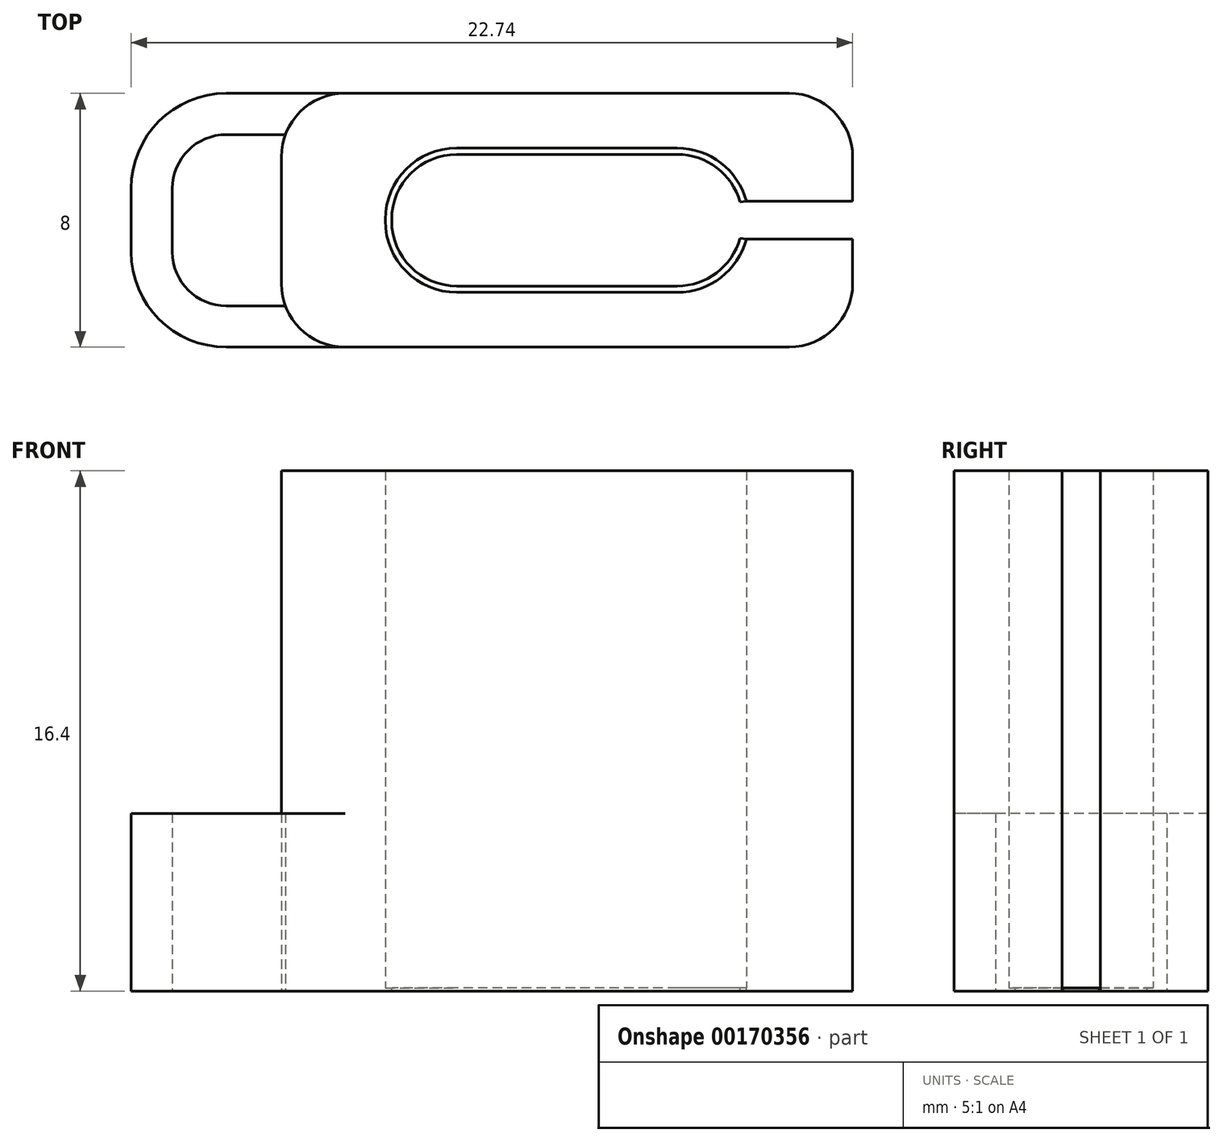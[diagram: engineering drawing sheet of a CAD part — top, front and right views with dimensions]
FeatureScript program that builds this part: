
annotation { "Feature Type Name" : "Feature", "Feature Type Description" : "" }
export const myFeature = defineFeature(function(context is Context, id is Id, definition is map)
    precondition{}
    {
        {
            var Q0;
            Q0=qCreatedBy(makeId("Top.planeOp"),FACE);
            var sketch = newSketch(context, id + "F0", { "sketchPlane" : qUnion([Q0])});
            skLineSegment(sketch, "E0.bottom", {"start": v(3.47, -2.27) * mm, "end": v(-3.47, -2.28) * mm});
            skLineSegment(sketch, "E0.top", {"start": v(3.47, 2.28) * mm, "end": v(-3.48, 2.27) * mm});
            skLineSegment(sketch, "E0.left", {"start": v(5.72, -0.02) * mm, "end": v(5.72, 0.03) * mm});
            skLineSegment(sketch, "E0.right", {"start": v(-5.72, -0.02) * mm, "end": v(-5.72, 0.02) * mm});
            skPoint(sketch, "E0.middle", {"position": v(0, 0) * mm});
            skPoint(sketch, "E1.visualSharp", {"position": v(-5.72, 2.27) * mm});
            skArc(sketch, "E1.filletArc", {"start": v(-3.48, 2.27) * mm, "mid": v(-5.07, 1.62) * mm, "end": v(-5.72, 0.02) * mm});
            skPoint(sketch, "E2.visualSharp", {"position": v(-5.72, -2.28) * mm});
            skArc(sketch, "E2.filletArc", {"start": v(-5.72, -0.03) * mm, "mid": v(-5.07, -1.62) * mm, "end": v(-3.47, -2.27) * mm});
            skPoint(sketch, "E3.visualSharp", {"position": v(5.72, -2.27) * mm});
            skArc(sketch, "E3.filletArc", {"start": v(3.47, -2.28) * mm, "mid": v(5.07, -1.62) * mm, "end": v(5.72, -0.02) * mm});
            skPoint(sketch, "E4.visualSharp", {"position": v(5.72, 2.28) * mm});
            skArc(sketch, "E4.filletArc", {"start": v(5.72, 0.03) * mm, "mid": v(5.07, 1.62) * mm, "end": v(3.47, 2.28) * mm});
            skLineSegment(sketch, "E5.bottom", {"start": v(4, -1.25) * mm, "end": v(-4, -1.25) * mm});
            skLineSegment(sketch, "E5.top", {"start": v(4, 1.25) * mm, "end": v(-4, 1.25) * mm});
            skLineSegment(sketch, "E5.left", {"start": v(4, -1.25) * mm, "end": v(4, 1.25) * mm});
            skLineSegment(sketch, "E5.right", {"start": v(-4, -1.25) * mm, "end": v(-4, 1.25) * mm});
            skSolve(sketch);
        }
        {
            var Q0;
            Q0=makeQuery(id+"F0.imprint","IMPRINT",FACE,{"disambiguationData":[TD([[makeQuery(id+"F0.imprint","IMPRINT",EDGE,{"derivedFrom":sQuery(id+"F0.wireOp",EDGE,"E0.bottom")}),-1.0]])]});
            var Q1;
            Q1=makeQuery(id+"F0.imprint","IMPRINT",FACE,{"disambiguationData":[TD([[makeQuery(id+"F0.imprint","IMPRINT",EDGE,{"derivedFrom":sQuery(id+"F0.wireOp",EDGE,"E5.bottom")}),-1.0]])]});
            extrude(context, id + "F1", {"entities" : qUnion([Q0, Q1]), "depth" : 16.25 * mm});
        }
        {
            var Q0;
            Q0=qCreatedBy(makeId("Top.planeOp"),FACE);
            var sketch = newSketch(context, id + "F2", { "sketchPlane" : qUnion([Q0])});
            skLineSegment(sketch, "E6.bottom", {"start": v(7, -4) * mm, "end": v(-7, -4) * mm});
            skLineSegment(sketch, "E6.top", {"start": v(7, 4) * mm, "end": v(-7, 4) * mm});
            skLineSegment(sketch, "E6.left", {"start": v(9, -2) * mm, "end": v(9, 2) * mm});
            skLineSegment(sketch, "E6.right", {"start": v(-9, -2) * mm, "end": v(-9, 2) * mm});
            skPoint(sketch, "E6.middle", {"position": v(0, 0) * mm});
            skPoint(sketch, "E7.visualSharp", {"position": v(-9, -4) * mm});
            skArc(sketch, "E7.filletArc", {"start": v(-9, -2) * mm, "mid": v(-8.41, -3.41) * mm, "end": v(-7, -4) * mm});
            skPoint(sketch, "E8.visualSharp", {"position": v(-9, 4) * mm});
            skArc(sketch, "E8.filletArc", {"start": v(-7, 4) * mm, "mid": v(-8.41, 3.41) * mm, "end": v(-9, 2) * mm});
            skPoint(sketch, "E9.visualSharp", {"position": v(9, -4) * mm});
            skArc(sketch, "E9.filletArc", {"start": v(7, -4) * mm, "mid": v(8.41, -3.41) * mm, "end": v(9, -2) * mm});
            skPoint(sketch, "E10.visualSharp", {"position": v(9, 4) * mm});
            skArc(sketch, "E10.filletArc", {"start": v(9, 2) * mm, "mid": v(8.41, 3.41) * mm, "end": v(7, 4) * mm});
            skLineSegment(sketch, "E11.bottom", {"start": v(-7, 4) * mm, "end": v(-10.74, 4) * mm});
            skLineSegment(sketch, "E11.top", {"start": v(-7, -4) * mm, "end": v(-10.74, -4) * mm});
            skLineSegment(sketch, "E11.left", {"start": v(-7, 4) * mm, "end": v(-7, -4) * mm});
            skLineSegment(sketch, "E11.right", {"start": v(-13.74, 1) * mm, "end": v(-13.74, -1) * mm});
            skPoint(sketch, "E12.visualSharp", {"position": v(-13.74, 4) * mm});
            skArc(sketch, "E12.filletArc", {"start": v(-10.74, 4) * mm, "mid": v(-12.86, 3.12) * mm, "end": v(-13.74, 1) * mm});
            skPoint(sketch, "E13.visualSharp", {"position": v(-13.74, -4) * mm});
            skArc(sketch, "E13.filletArc", {"start": v(-13.74, -1) * mm, "mid": v(-12.86, -3.12) * mm, "end": v(-10.74, -4) * mm});
            skArc(sketch, "E14.0", {"start": v(-12.44, -1) * mm, "mid": v(-11.94, -2.2) * mm, "end": v(-10.74, -2.7) * mm});
            skLineSegment(sketch, "E14.1", {"start": v(-12.44, 1) * mm, "end": v(-12.44, -1) * mm});
            skArc(sketch, "E14.2", {"start": v(-10.74, 2.7) * mm, "mid": v(-11.94, 2.2) * mm, "end": v(-12.44, 1) * mm});
            skLineSegment(sketch, "E15", {"start": v(-10.74, 2.7) * mm, "end": v(-7.92, 2.7) * mm});
            skLineSegment(sketch, "E16", {"start": v(-7.92, 2.7) * mm, "end": v(-7.92, -2.7) * mm});
            skLineSegment(sketch, "E17", {"start": v(-7.92, -2.7) * mm, "end": v(-10.74, -2.7) * mm});
            skSolve(sketch);
        }
        {
            var Q0;
            Q0=makeQuery(id+"F2.imprint","IMPRINT",FACE,{"disambiguationData":[TD([[makeQuery(id+"F2.imprint","IMPRINT",EDGE,{"derivedFrom":sQuery(id+"F2.wireOp",EDGE,"E6.bottom")}),-1.0]])]});
            var Q1;
            Q1=makeQuery(id+"F2.imprint","IMPRINT",FACE,{"disambiguationData":[TD([[makeQuery(id+"F2.imprint","IMPRINT",EDGE,{"derivedFrom":sQuery(id+"F2.wireOp",EDGE,"E6.right")}),-1.0]])]});
            var Q2;
            {var subQ0=sQuery(id+"F2.wireOp",EDGE,"E11.left");Q2=makeQuery(id+"F2.imprint","IMPRINT",FACE,{"disambiguationData":[TD([[makeQuery(id+"F2.imprint","IMPRINT",EDGE,{"derivedFrom":subQ0}),-1.0]])]});}
            extrude(context, id + "F3", {"entities" : qUnion([Q0, Q1, Q2]), "depth" : 16.2 * mm});
        }
        {
            var Q0;
            {var subQ0=sQuery(id+"F2.wireOp",EDGE,"E6.left");Q0=makeQuery(id+"FNUhWBLdZuZYwrX_2.boolean.opBoolean","MERGE",FACE,{"derivedFrom":[makeQuery(id+"F3.opExtrude","SWEPT_FACE",FACE,{"disambiguationData":[OSD([subQ0])]}),makeQuery(id+"FNUhWBLdZuZYwrX_2.opExtrude","SWEPT_FACE",FACE,{"disambiguationData":[OSD([subQ0])]})]});}
            var sketch = newSketch(context, id + "F4", { "sketchPlane" : qUnion([Q0])});
            skSolve(sketch);
        }
        {
            var Q0;
            {var subQ0=sQuery(id+"F2.wireOp",EDGE,"E6.left");Q0=makeQuery(id+"F4.imprint","IMPRINT",FACE,{"disambiguationData":[TD([[makeQuery(id+"F4.imprint","IMPRINT",EDGE,{"derivedFrom":makeQuery(id+"F3.opExtrude","CAP_EDGE",EDGE,{"disambiguationData":[OSD([subQ0])],"isStart":false})}),-1.0]])]});}
            var sketch = newSketch(context, id + "F5", { "sketchPlane" : qUnion([Q0])});
            skLineSegment(sketch, "E18.bottom", {"start": v(0.6, -1) * mm, "end": v(-0.6, -1) * mm});
            skLineSegment(sketch, "E18.top", {"start": v(0.6, 17) * mm, "end": v(-0.6, 17) * mm});
            skLineSegment(sketch, "E18.left", {"start": v(0.6, -1) * mm, "end": v(0.6, 17) * mm});
            skLineSegment(sketch, "E18.right", {"start": v(-0.6, -1) * mm, "end": v(-0.6, 17) * mm});
            skPoint(sketch, "E18.middle", {"position": v(0, 8) * mm});
            skLineSegment(sketch, "E19", {"start": v(-0.6, -1) * mm, "end": v(0.6, -1) * mm});
            skLineSegment(sketch, "E20", {"start": v(-0.6, 17) * mm, "end": v(0.6, 17) * mm});
            skSolve(sketch);
        }
        {
            var Q0;
            Q0=makeQuery(id+"F1.opExtrude","SWEPT_BODY",BODY,{"disambiguationData":[OSD([sQuery(id+"F0.wireOp",EDGE,"E0.bottom"),sQuery(id+"F0.wireOp",EDGE,"E0.top"),sQuery(id+"F0.wireOp",EDGE,"E0.left"),sQuery(id+"F0.wireOp",EDGE,"E0.right"),sQuery(id+"F0.wireOp",EDGE,"E1.filletArc"),sQuery(id+"F0.wireOp",EDGE,"E2.filletArc"),sQuery(id+"F0.wireOp",EDGE,"E3.filletArc"),sQuery(id+"F0.wireOp",EDGE,"E4.filletArc"),sQuery(id+"F0.wireOp",EDGE,"E5.bottom"),sQuery(id+"F0.wireOp",EDGE,"E5.top"),sQuery(id+"F0.wireOp",EDGE,"E5.left"),sQuery(id+"F0.wireOp",EDGE,"E5.right")])]});
            var Q1;
            Q1=makeQuery(id+"F3.opExtrude","SWEPT_BODY",BODY,{"disambiguationData":[OSD([sQuery(id+"F2.wireOp",EDGE,"E6.bottom"),sQuery(id+"F2.wireOp",EDGE,"E6.top"),sQuery(id+"F2.wireOp",EDGE,"E6.left"),sQuery(id+"F2.wireOp",EDGE,"E6.right"),sQuery(id+"F2.wireOp",EDGE,"E7.filletArc"),sQuery(id+"F2.wireOp",EDGE,"E8.filletArc"),sQuery(id+"F2.wireOp",EDGE,"E9.filletArc"),sQuery(id+"F2.wireOp",EDGE,"E10.filletArc")])]});
            booleanBodies(context, id + "F6", {"operationType" : BooleanOperationType.SUBTRACTION, "tools" : qUnion([Q0]), "targets" : qUnion([Q1])});
        }
        {
            var Q0;
            Q0 = qSketchRegion(id + "F5", true);
            extrude(context, id + "F7", {"entities" : qUnion([Q0]), "operationType" : NewBodyOperationType.REMOVE, "endBound" : BoundingType.UP_TO_NEXT, "oppositeDirection" : true, "depth" : 25 * mm});
        }
        {
            var Q0;
            {var subQ6=sQuery(id+"F2.wireOp",EDGE,"E11.bottom");Q0=makeQuery(id+"F2.imprint","IMPRINT",FACE,{"disambiguationData":[TD([[makeQuery(id+"F2.imprint","IMPRINT",EDGE,{"derivedFrom":subQ6}),1.0]])]});}
            extrude(context, id + "F8", {"entities" : qUnion([Q0]), "operationType" : NewBodyOperationType.ADD, "depth" : 5.5 * mm});
        }
        {
            var Q0;
            Q0=makeQuery(id+"F3.opExtrude","CAP_FACE",FACE,{"disambiguationData":[OSD([sQuery(id+"F2.wireOp",EDGE,"E6.bottom"),sQuery(id+"F2.wireOp",EDGE,"E6.top"),sQuery(id+"F2.wireOp",EDGE,"E6.left"),sQuery(id+"F2.wireOp",EDGE,"E6.right"),sQuery(id+"F2.wireOp",EDGE,"E7.filletArc"),sQuery(id+"F2.wireOp",EDGE,"E8.filletArc"),sQuery(id+"F2.wireOp",EDGE,"E9.filletArc"),sQuery(id+"F2.wireOp",EDGE,"E10.filletArc")])],"isStart":false});
            var sketch = newSketch(context, id + "F9", { "sketchPlane" : qUnion([Q0])});
            skArc(sketch, "E21.0", {"start": v(-3.47, -2.08) * mm, "mid": v(-4.92, -1.47) * mm, "end": v(-5.53, -0.03) * mm});
            skLineSegment(sketch, "E21.1", {"start": v(-3.47, -2.08) * mm, "end": v(3.47, -2.08) * mm});
            skArc(sketch, "E21.2", {"start": v(5.45, -0.57) * mm, "mid": v(4.72, -1.66) * mm, "end": v(3.47, -2.08) * mm});
            skArc(sketch, "E21.3", {"start": v(-5.53, 0.02) * mm, "mid": v(-4.92, 1.47) * mm, "end": v(-3.48, 2.08) * mm});
            skLineSegment(sketch, "E21.4", {"start": v(-3.48, 2.08) * mm, "end": v(3.47, 2.08) * mm});
            skArc(sketch, "E21.5", {"start": v(3.47, 2.08) * mm, "mid": v(4.72, 1.66) * mm, "end": v(5.45, 0.57) * mm});
            skArc(sketch, "E22.0", {"start": v(-7, 4) * mm, "mid": v(-8.41, 3.41) * mm, "end": v(-9, 2) * mm});
            skLineSegment(sketch, "E22.1", {"start": v(7, 4) * mm, "end": v(-7, 4) * mm});
            skLineSegment(sketch, "E22.2", {"start": v(-9, -2) * mm, "end": v(-9, 2) * mm});
            skArc(sketch, "E22.3", {"start": v(-9, -2) * mm, "mid": v(-8.41, -3.41) * mm, "end": v(-7, -4) * mm});
            skLineSegment(sketch, "E22.4", {"start": v(7, -4) * mm, "end": v(-7, -4) * mm});
            skArc(sketch, "E22.5", {"start": v(7, -4) * mm, "mid": v(8.41, -3.41) * mm, "end": v(9, -2) * mm});
            skLineSegment(sketch, "E22.6", {"start": v(9, -2) * mm, "end": v(9, -0.6) * mm});
            skArc(sketch, "E22.7", {"start": v(9, 2) * mm, "mid": v(8.41, 3.41) * mm, "end": v(7, 4) * mm});
            skLineSegment(sketch, "E22.8", {"start": v(9, 0.6) * mm, "end": v(9, 2) * mm});
            skLineSegment(sketch, "E23.0", {"start": v(5.65, 0.6) * mm, "end": v(9, 0.6) * mm});
            skLineSegment(sketch, "E24.0", {"start": v(5.65, -0.6) * mm, "end": v(9, -0.6) * mm});
            skLineSegment(sketch, "E25", {"start": v(5.65, 0.6) * mm, "end": v(5.45, 0.57) * mm});
            skLineSegment(sketch, "E26", {"start": v(5.65, -0.6) * mm, "end": v(5.45, -0.57) * mm});
            skLineSegment(sketch, "E27", {"start": v(-5.53, -0.03) * mm, "end": v(-5.53, 0.02) * mm});
            skSolve(sketch);
        }
        {
            var Q0;
            Q0=makeQuery(id+"F9.imprint","IMPRINT",FACE,{"disambiguationData":[TD([[makeQuery(id+"F9.imprint","IMPRINT",EDGE,{"derivedFrom":sQuery(id+"F9.wireOp",EDGE,"E21.0")}),1.0]])]});
            var Q1;
            Q1=makeQuery(id+"F9.imprint","IMPRINT",FACE,{"disambiguationData":[TD([[makeQuery(id+"F9.imprint","IMPRINT",EDGE,{"derivedFrom":sQuery(id+"F9.wireOp",EDGE,"E22.0")}),1.0]])]});
            extrude(context, id + "F10", {"entities" : qUnion([Q0, Q1]), "operationType" : NewBodyOperationType.ADD, "depth" : 0.1 * mm});
        }
        {
            var Q0;
            {var subQ0=sQuery(id+"F2.wireOp",EDGE,"E8.filletArc");var subQ1=sQuery(id+"F2.wireOp",EDGE,"E7.filletArc");Q0=makeQuery(id+"F8.boolean.opBoolean","MERGE",FACE,{"derivedFrom":[makeQuery(id+"F3.opExtrude","CAP_FACE",FACE,{"disambiguationData":[OSD([sQuery(id+"F2.wireOp",EDGE,"E6.bottom"),sQuery(id+"F2.wireOp",EDGE,"E6.top"),sQuery(id+"F2.wireOp",EDGE,"E6.left"),sQuery(id+"F2.wireOp",EDGE,"E6.right"),subQ1,subQ0,sQuery(id+"F2.wireOp",EDGE,"E9.filletArc"),sQuery(id+"F2.wireOp",EDGE,"E10.filletArc")])],"isStart":true}),makeQuery(id+"F8.opExtrude","CAP_FACE",FACE,{"disambiguationData":[OSD([subQ1,subQ0,sQuery(id+"F2.wireOp",EDGE,"E11.bottom"),sQuery(id+"F2.wireOp",EDGE,"E11.top"),sQuery(id+"F2.wireOp",EDGE,"E11.right"),sQuery(id+"F2.wireOp",EDGE,"E12.filletArc"),sQuery(id+"F2.wireOp",EDGE,"E13.filletArc"),sQuery(id+"F2.wireOp",EDGE,"E14.0"),sQuery(id+"F2.wireOp",EDGE,"E14.1"),sQuery(id+"F2.wireOp",EDGE,"E14.2"),sQuery(id+"F2.wireOp",EDGE,"E15"),sQuery(id+"F2.wireOp",EDGE,"E17")])],"isStart":true})]});}
            var sketch = newSketch(context, id + "F11", { "sketchPlane" : qUnion([Q0])});
            skArc(sketch, "E28.0", {"start": v(3.47, -2.08) * mm, "mid": v(4.72, -1.66) * mm, "end": v(5.45, -0.57) * mm});
            skLineSegment(sketch, "E28.1", {"start": v(-3.48, -2.08) * mm, "end": v(3.47, -2.08) * mm});
            skArc(sketch, "E28.2", {"start": v(-5.53, -0.02) * mm, "mid": v(-4.92, -1.47) * mm, "end": v(-3.48, -2.08) * mm});
            skArc(sketch, "E28.3", {"start": v(-3.47, 2.08) * mm, "mid": v(-4.92, 1.47) * mm, "end": v(-5.53, 0.03) * mm});
            skLineSegment(sketch, "E28.4", {"start": v(-3.47, 2.08) * mm, "end": v(3.47, 2.08) * mm});
            skArc(sketch, "E28.5", {"start": v(5.45, 0.57) * mm, "mid": v(4.72, 1.66) * mm, "end": v(3.47, 2.08) * mm});
            skLineSegment(sketch, "E29.2", {"start": v(-5.53, 0.03) * mm, "end": v(-5.53, -0.02) * mm});
            skLineSegment(sketch, "E30.0", {"start": v(5.65, -0.6) * mm, "end": v(9, -0.6) * mm});
            skLineSegment(sketch, "E31.0", {"start": v(5.65, 0.6) * mm, "end": v(9, 0.6) * mm});
            skLineSegment(sketch, "E32.0", {"start": v(5.65, 0.6) * mm, "end": v(5.45, 0.57) * mm});
            skLineSegment(sketch, "E33.0", {"start": v(5.65, -0.6) * mm, "end": v(5.45, -0.57) * mm});
            skLineSegment(sketch, "E34.0", {"start": v(9, 2) * mm, "end": v(9, 0.6) * mm});
            skArc(sketch, "E35.0", {"start": v(7, 4) * mm, "mid": v(8.41, 3.41) * mm, "end": v(9, 2) * mm});
            skLineSegment(sketch, "E36.0", {"start": v(9, -0.6) * mm, "end": v(9, -2) * mm});
            skArc(sketch, "E37.0", {"start": v(9, -2) * mm, "mid": v(8.41, -3.41) * mm, "end": v(7, -4) * mm});
            skLineSegment(sketch, "E38.0", {"start": v(7, -4) * mm, "end": v(-7, -4) * mm});
            skArc(sketch, "E39.0", {"start": v(-10.74, -4) * mm, "mid": v(-12.86, -3.12) * mm, "end": v(-13.74, -1) * mm});
            skLineSegment(sketch, "E40.0", {"start": v(-7, -4) * mm, "end": v(-10.74, -4) * mm});
            skLineSegment(sketch, "E41.0", {"start": v(-13.74, -1) * mm, "end": v(-13.74, 1) * mm});
            skArc(sketch, "E42.0", {"start": v(-13.74, 1) * mm, "mid": v(-12.86, 3.12) * mm, "end": v(-10.74, 4) * mm});
            skLineSegment(sketch, "E43.0", {"start": v(7, 4) * mm, "end": v(-7, 4) * mm});
            skLineSegment(sketch, "E44.0", {"start": v(-7, 4) * mm, "end": v(-10.74, 4) * mm});
            skSolve(sketch);
        }
        {
            var Q0;
            Q0=makeQuery(id+"F11.imprint","IMPRINT",FACE,{"disambiguationData":[TD([[makeQuery(id+"F11.imprint","IMPRINT",EDGE,{"derivedFrom":sQuery(id+"F11.wireOp",EDGE,"E28.0")}),-1.0]])]});
            var Q1;
            Q1=makeQuery(id+"F11.imprint","IMPRINT",FACE,{"disambiguationData":[TD([[makeQuery(id+"F11.imprint","IMPRINT",EDGE,{"derivedFrom":sQuery(id+"F11.wireOp",EDGE,"E30.0")}),-1.0]])]});
            extrude(context, id + "F12", {"entities" : qUnion([Q0, Q1]), "operationType" : NewBodyOperationType.ADD, "depth" : 0.1 * mm});
        }
    });
